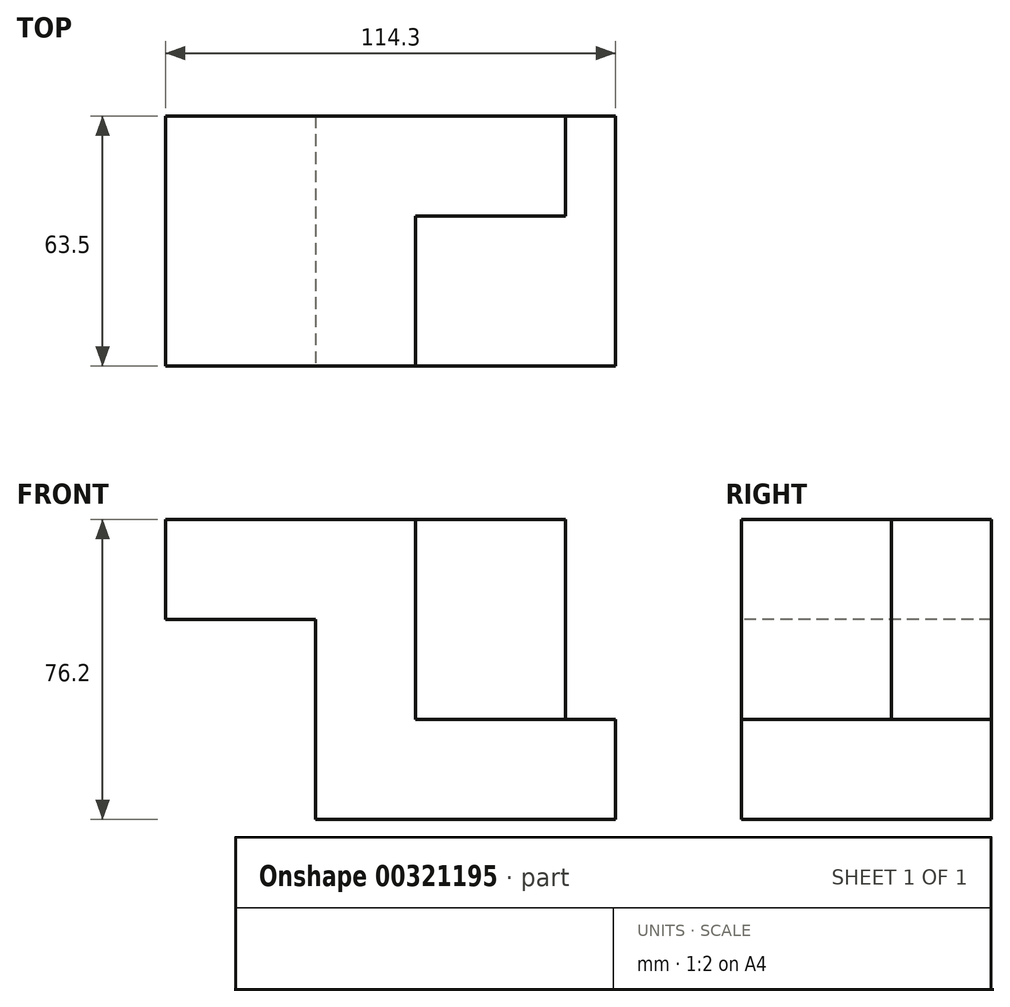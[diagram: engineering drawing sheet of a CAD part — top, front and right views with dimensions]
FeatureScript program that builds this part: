
annotation { "Feature Type Name" : "Feature", "Feature Type Description" : "" }
export const myFeature = defineFeature(function(context is Context, id is Id, definition is map)
    precondition{}
    {
        {
            var Q0;
            Q0=qCreatedBy(makeId("Front.planeOp"),FACE);
            var sketch = newSketch(context, id + "F0", { "sketchPlane" : qUnion([Q0])});
            skLineSegment(sketch, "E0", {"start": v(-61.35, 8.36) * mm, "end": v(-61.35, -17.04) * mm});
            skLineSegment(sketch, "E1", {"start": v(-61.35, -17.04) * mm, "end": v(-23.25, -17.04) * mm});
            skLineSegment(sketch, "E2", {"start": v(-23.25, -17.04) * mm, "end": v(-23.25, -67.84) * mm});
            skLineSegment(sketch, "E3", {"start": v(-23.25, -67.84) * mm, "end": v(52.95, -67.84) * mm});
            skLineSegment(sketch, "E4", {"start": v(52.95, -67.84) * mm, "end": v(52.95, -42.44) * mm});
            skLineSegment(sketch, "E5", {"start": v(52.95, -42.44) * mm, "end": v(2.15, -42.44) * mm});
            skLineSegment(sketch, "E6", {"start": v(2.15, -42.44) * mm, "end": v(2.15, 8.36) * mm});
            skLineSegment(sketch, "E7", {"start": v(2.15, 8.36) * mm, "end": v(-61.35, 8.36) * mm});
            skSolve(sketch);
        }
        {
            var Q0;
            Q0=makeQuery(id+"F0.imprint","IMPRINT",FACE,{"disambiguationData":[TD([[makeQuery(id+"F0.imprint","IMPRINT",EDGE,{"derivedFrom":sQuery(id+"F0.wireOp",EDGE,"E0")}),1.0]])]});
            extrude(context, id + "F1", {"entities" : qUnion([Q0]), "oppositeDirection" : true, "depth" : 63.5 * mm});
        }
        {
            var Q0;
            Q0=makeQuery(id+"F1.opExtrude","SWEPT_FACE",FACE,{"disambiguationData":[OSD([sQuery(id+"F0.wireOp",EDGE,"E5")])]});
            var sketch = newSketch(context, id + "F2", { "sketchPlane" : qUnion([Q0])});
            skLineSegment(sketch, "E8.bottom", {"start": v(2.15, 63.5) * mm, "end": v(40.25, 63.5) * mm});
            skLineSegment(sketch, "E8.top", {"start": v(2.15, 38.1) * mm, "end": v(40.25, 38.1) * mm});
            skLineSegment(sketch, "E8.left", {"start": v(2.15, 63.5) * mm, "end": v(2.15, 38.1) * mm});
            skLineSegment(sketch, "E8.right", {"start": v(40.25, 63.5) * mm, "end": v(40.25, 38.1) * mm});
            skSolve(sketch);
        }
        {
            var Q0;
            Q0=makeQuery(id+"F2.imprint","IMPRINT",FACE,{"disambiguationData":[TD([[makeQuery(id+"F2.imprint","IMPRINT",EDGE,{"derivedFrom":sQuery(id+"F2.wireOp",EDGE,"E8.bottom")}),1.0]])]});
            extrude(context, id + "F3", {"entities" : qUnion([Q0]), "operationType" : NewBodyOperationType.ADD, "depth" : 50.8 * mm});
        }
    });
